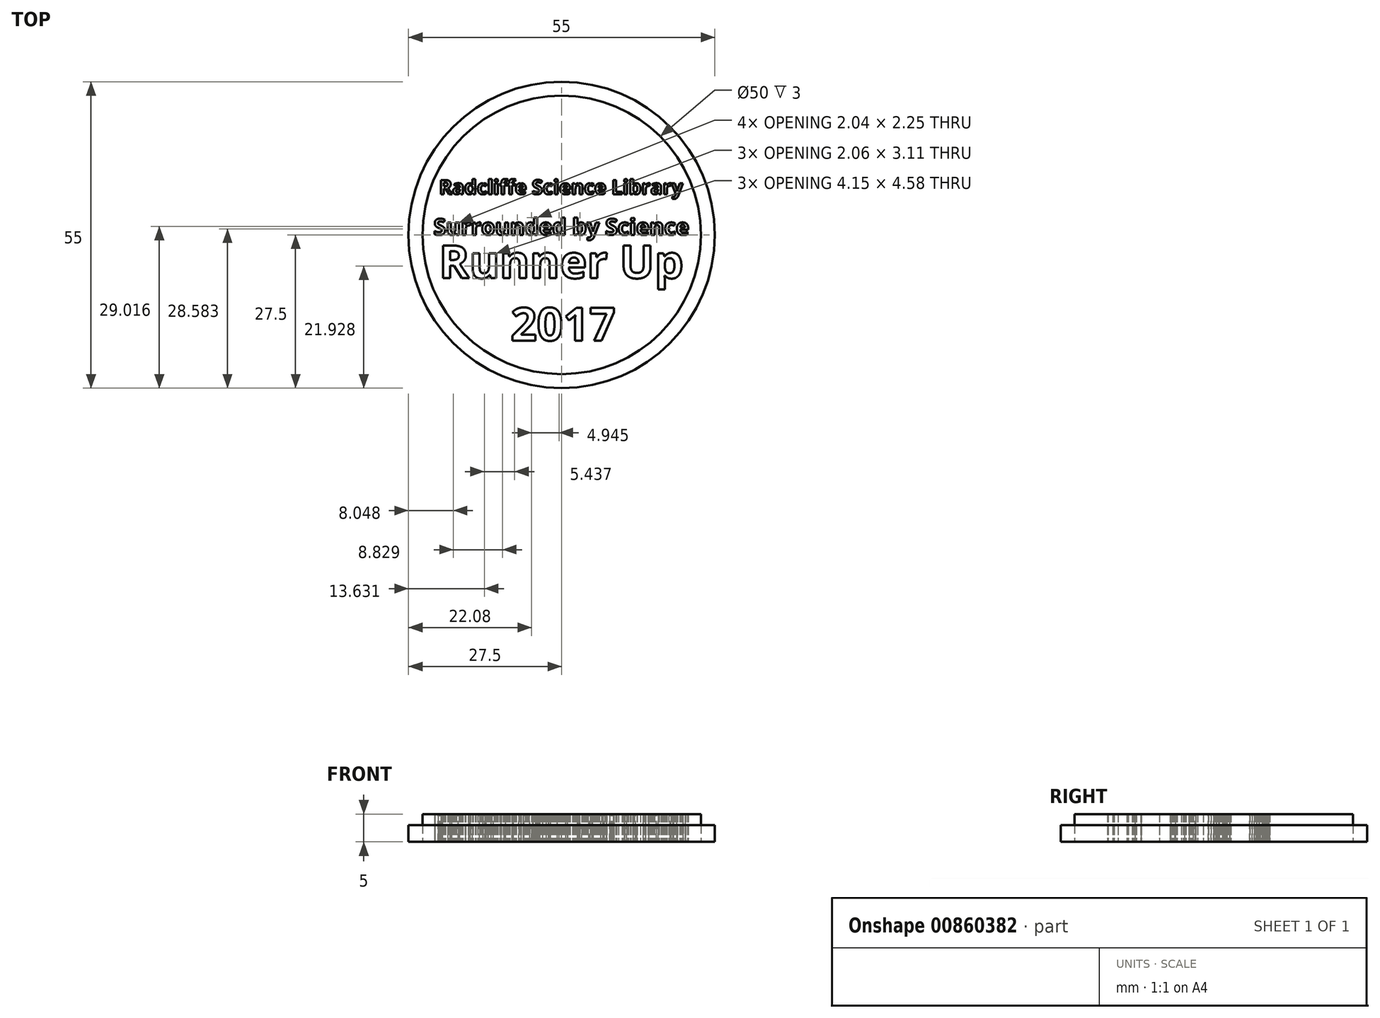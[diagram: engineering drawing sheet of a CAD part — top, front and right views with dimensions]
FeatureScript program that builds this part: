
annotation { "Feature Type Name" : "Feature", "Feature Type Description" : "" }
export const myFeature = defineFeature(function(context is Context, id is Id, definition is map)
    precondition{}
    {
        {
            var Q0;
            Q0=qCreatedBy(makeId("Top.planeOp"),FACE);
            var sketch = newSketch(context, id + "F0", { "sketchPlane" : qUnion([Q0])});
            skCircle(sketch, "E0", {"center": v(0, 0) * mm, "radius": 27.5 * mm});
            skCircle(sketch, "E1", {"center": v(0, 0) * mm, "radius": 25 * mm});
            skText(sketch, "E2", { "text": "Surrounded by Science", "fontName": "OpenSans-Bold.ttf"});
            skText(sketch, "E3", { "text": "Radcliffe Science Library", "fontName": "OpenSans-Bold.ttf"});
            skText(sketch, "E4", { "text": "Runner Up\n      2017     ", "fontName": "OpenSans-Bold.ttf"});
            const initialGuessF0  = {"E2": [-0.023, 0, 1, 0, 0.00291], "E3": [-0.022, 0.0073, 1, 0, 0.00258], "E4": [-0.022, -0.00778, 1, 0, 0.00593]};
            skSetInitialGuess(sketch, initialGuessF0);
            skSolve(sketch);
        }
        {
            var Q0;
            Q0=makeQuery(id+"F0.imprint","IMPRINT",FACE,{"disambiguationData":[TD([[makeQuery(id+"F0.imprint","IMPRINT",EDGE,{"derivedFrom":sQuery(id+"F0.wireOp",EDGE,"E1")}),1.0]])]});
            var Q1;
            Q1=makeQuery(id+"F0.imprint","IMPRINT",FACE,{"disambiguationData":[TD([[makeQuery(id+"F0.imprint","IMPRINT",EDGE,{"derivedFrom":sQuery(id+"F0.wireOp",EDGE,"E4.sketch_text.stroke-173")}),1.0]])]});
            var Q2;
            Q2=makeQuery(id+"F0.imprint","IMPRINT",FACE,{"disambiguationData":[TD([[makeQuery(id+"F0.imprint","IMPRINT",EDGE,{"derivedFrom":sQuery(id+"F0.wireOp",EDGE,"E4.sketch_text.stroke-70")}),1.0]])]});
            var Q3;
            Q3=makeQuery(id+"F0.imprint","IMPRINT",FACE,{"disambiguationData":[TD([[makeQuery(id+"F0.imprint","IMPRINT",EDGE,{"derivedFrom":sQuery(id+"F0.wireOp",EDGE,"E4.sketch_text.stroke-133")}),1.0]])]});
            var Q4;
            Q4=makeQuery(id+"F0.imprint","IMPRINT",FACE,{"disambiguationData":[TD([[makeQuery(id+"F0.imprint","IMPRINT",EDGE,{"derivedFrom":sQuery(id+"F0.wireOp",EDGE,"E4.sketch_text.stroke-0")}),1.0]])]});
            var Q5;
            Q5=makeQuery(id+"F0.imprint","IMPRINT",FACE,{"disambiguationData":[TD([[makeQuery(id+"F0.imprint","IMPRINT",EDGE,{"derivedFrom":sQuery(id+"F0.wireOp",EDGE,"E2.sketch_text.stroke-71")}),1.0]])]});
            var Q6;
            Q6=makeQuery(id+"F0.imprint","IMPRINT",FACE,{"disambiguationData":[TD([[makeQuery(id+"F0.imprint","IMPRINT",EDGE,{"derivedFrom":sQuery(id+"F0.wireOp",EDGE,"E2.sketch_text.stroke-137")}),1.0]])]});
            var Q7;
            Q7=makeQuery(id+"F0.imprint","IMPRINT",FACE,{"disambiguationData":[TD([[makeQuery(id+"F0.imprint","IMPRINT",EDGE,{"derivedFrom":sQuery(id+"F0.wireOp",EDGE,"E2.sketch_text.stroke-146")}),1.0]])]});
            var Q8;
            Q8=makeQuery(id+"F0.imprint","IMPRINT",FACE,{"disambiguationData":[TD([[makeQuery(id+"F0.imprint","IMPRINT",EDGE,{"derivedFrom":sQuery(id+"F0.wireOp",EDGE,"E2.sketch_text.stroke-180")}),1.0]])]});
            var Q9;
            Q9=makeQuery(id+"F0.imprint","IMPRINT",FACE,{"disambiguationData":[TD([[makeQuery(id+"F0.imprint","IMPRINT",EDGE,{"derivedFrom":sQuery(id+"F0.wireOp",EDGE,"E2.sketch_text.stroke-203")}),1.0]])]});
            var Q10;
            Q10=makeQuery(id+"F0.imprint","IMPRINT",FACE,{"disambiguationData":[TD([[makeQuery(id+"F0.imprint","IMPRINT",EDGE,{"derivedFrom":sQuery(id+"F0.wireOp",EDGE,"E2.sketch_text.stroke-280")}),1.0]])]});
            var Q11;
            Q11=makeQuery(id+"F0.imprint","IMPRINT",FACE,{"disambiguationData":[TD([[makeQuery(id+"F0.imprint","IMPRINT",EDGE,{"derivedFrom":sQuery(id+"F0.wireOp",EDGE,"E2.sketch_text.stroke-331")}),1.0]])]});
            var Q12;
            Q12=makeQuery(id+"F0.imprint","IMPRINT",FACE,{"disambiguationData":[TD([[makeQuery(id+"F0.imprint","IMPRINT",EDGE,{"derivedFrom":sQuery(id+"F0.wireOp",EDGE,"E3.sketch_text.stroke-341")}),1.0]])]});
            var Q13;
            Q13=makeQuery(id+"F0.imprint","IMPRINT",FACE,{"disambiguationData":[TD([[makeQuery(id+"F0.imprint","IMPRINT",EDGE,{"derivedFrom":sQuery(id+"F0.wireOp",EDGE,"E3.sketch_text.stroke-301")}),1.0]])]});
            var Q14;
            Q14=makeQuery(id+"F0.imprint","IMPRINT",FACE,{"disambiguationData":[TD([[makeQuery(id+"F0.imprint","IMPRINT",EDGE,{"derivedFrom":sQuery(id+"F0.wireOp",EDGE,"E3.sketch_text.stroke-252")}),1.0]])]});
            var Q15;
            Q15=makeQuery(id+"F0.imprint","IMPRINT",FACE,{"disambiguationData":[TD([[makeQuery(id+"F0.imprint","IMPRINT",EDGE,{"derivedFrom":sQuery(id+"F0.wireOp",EDGE,"E3.sketch_text.stroke-201")}),1.0]])]});
            var Q16;
            Q16=makeQuery(id+"F0.imprint","IMPRINT",FACE,{"disambiguationData":[TD([[makeQuery(id+"F0.imprint","IMPRINT",EDGE,{"derivedFrom":sQuery(id+"F0.wireOp",EDGE,"E3.sketch_text.stroke-130")}),1.0]])]});
            var Q17;
            Q17=makeQuery(id+"F0.imprint","IMPRINT",FACE,{"disambiguationData":[TD([[makeQuery(id+"F0.imprint","IMPRINT",EDGE,{"derivedFrom":sQuery(id+"F0.wireOp",EDGE,"E3.sketch_text.stroke-58")}),1.0]])]});
            var Q18;
            Q18=makeQuery(id+"F0.imprint","IMPRINT",FACE,{"disambiguationData":[TD([[makeQuery(id+"F0.imprint","IMPRINT",EDGE,{"derivedFrom":sQuery(id+"F0.wireOp",EDGE,"E3.sketch_text.stroke-37")}),1.0]])]});
            var Q19;
            Q19=makeQuery(id+"F0.imprint","IMPRINT",FACE,{"disambiguationData":[TD([[makeQuery(id+"F0.imprint","IMPRINT",EDGE,{"derivedFrom":sQuery(id+"F0.wireOp",EDGE,"E3.sketch_text.stroke-0")}),1.0]])]});
            extrude(context, id + "F1", {"entities" : qUnion([Q0, Q1, Q2, Q3, Q4, Q5, Q6, Q7, Q8, Q9, Q10, Q11, Q12, Q13, Q14, Q15, Q16, Q17, Q18, Q19]), "depth" : 5 * mm, "offsetDistance" : 25 * mm});
        }
        {
            var Q0;
            Q0=makeQuery(id+"F0.imprint","IMPRINT",FACE,{"disambiguationData":[TD([[makeQuery(id+"F0.imprint","IMPRINT",EDGE,{"derivedFrom":sQuery(id+"F0.wireOp",EDGE,"E0")}),1.0]])]});
            var Q1;
            Q1=makeQuery(id+"F0.imprint","IMPRINT",FACE,{"disambiguationData":[TD([[makeQuery(id+"F0.imprint","IMPRINT",EDGE,{"derivedFrom":sQuery(id+"F0.wireOp",EDGE,"E4.sketch_text.stroke-141")}),-1.0]])]});
            var Q2;
            Q2=makeQuery(id+"F0.imprint","IMPRINT",FACE,{"disambiguationData":[TD([[makeQuery(id+"F0.imprint","IMPRINT",EDGE,{"derivedFrom":sQuery(id+"F0.wireOp",EDGE,"E4.sketch_text.stroke-165")}),-1.0]])]});
            var Q3;
            Q3=makeQuery(id+"F0.imprint","IMPRINT",FACE,{"disambiguationData":[TD([[makeQuery(id+"F0.imprint","IMPRINT",EDGE,{"derivedFrom":sQuery(id+"F0.wireOp",EDGE,"E4.sketch_text.stroke-181")}),-1.0]])]});
            var Q4;
            Q4=makeQuery(id+"F0.imprint","IMPRINT",FACE,{"disambiguationData":[TD([[makeQuery(id+"F0.imprint","IMPRINT",EDGE,{"derivedFrom":sQuery(id+"F0.wireOp",EDGE,"E4.sketch_text.stroke-191")}),-1.0]])]});
            var Q5;
            Q5=makeQuery(id+"F0.imprint","IMPRINT",FACE,{"disambiguationData":[TD([[makeQuery(id+"F0.imprint","IMPRINT",EDGE,{"derivedFrom":sQuery(id+"F0.wireOp",EDGE,"E4.sketch_text.stroke-118")}),-1.0]])]});
            var Q6;
            Q6=makeQuery(id+"F0.imprint","IMPRINT",FACE,{"disambiguationData":[TD([[makeQuery(id+"F0.imprint","IMPRINT",EDGE,{"derivedFrom":sQuery(id+"F0.wireOp",EDGE,"E4.sketch_text.stroke-103")}),-1.0]])]});
            var Q7;
            Q7=makeQuery(id+"F0.imprint","IMPRINT",FACE,{"disambiguationData":[TD([[makeQuery(id+"F0.imprint","IMPRINT",EDGE,{"derivedFrom":sQuery(id+"F0.wireOp",EDGE,"E4.sketch_text.stroke-90")}),-1.0]])]});
            var Q8;
            Q8=makeQuery(id+"F0.imprint","IMPRINT",FACE,{"disambiguationData":[TD([[makeQuery(id+"F0.imprint","IMPRINT",EDGE,{"derivedFrom":sQuery(id+"F0.wireOp",EDGE,"E4.sketch_text.stroke-70")}),-1.0]])]});
            var Q9;
            Q9=makeQuery(id+"F0.imprint","IMPRINT",FACE,{"disambiguationData":[TD([[makeQuery(id+"F0.imprint","IMPRINT",EDGE,{"derivedFrom":sQuery(id+"F0.wireOp",EDGE,"E4.sketch_text.stroke-53")}),-1.0]])]});
            var Q10;
            Q10=makeQuery(id+"F0.imprint","IMPRINT",FACE,{"disambiguationData":[TD([[makeQuery(id+"F0.imprint","IMPRINT",EDGE,{"derivedFrom":sQuery(id+"F0.wireOp",EDGE,"E4.sketch_text.stroke-36")}),-1.0]])]});
            var Q11;
            Q11=makeQuery(id+"F0.imprint","IMPRINT",FACE,{"disambiguationData":[TD([[makeQuery(id+"F0.imprint","IMPRINT",EDGE,{"derivedFrom":sQuery(id+"F0.wireOp",EDGE,"E4.sketch_text.stroke-19")}),-1.0]])]});
            var Q12;
            Q12=makeQuery(id+"F0.imprint","IMPRINT",FACE,{"disambiguationData":[TD([[makeQuery(id+"F0.imprint","IMPRINT",EDGE,{"derivedFrom":sQuery(id+"F0.wireOp",EDGE,"E4.sketch_text.stroke-0")}),-1.0]])]});
            var Q13;
            Q13=makeQuery(id+"F0.imprint","IMPRINT",FACE,{"disambiguationData":[TD([[makeQuery(id+"F0.imprint","IMPRINT",EDGE,{"derivedFrom":sQuery(id+"F0.wireOp",EDGE,"E2.sketch_text.stroke-0")}),-1.0]])]});
            var Q14;
            Q14=makeQuery(id+"F0.imprint","IMPRINT",FACE,{"disambiguationData":[TD([[makeQuery(id+"F0.imprint","IMPRINT",EDGE,{"derivedFrom":sQuery(id+"F0.wireOp",EDGE,"E2.sketch_text.stroke-28")}),-1.0]])]});
            var Q15;
            Q15=makeQuery(id+"F0.imprint","IMPRINT",FACE,{"disambiguationData":[TD([[makeQuery(id+"F0.imprint","IMPRINT",EDGE,{"derivedFrom":sQuery(id+"F0.wireOp",EDGE,"E2.sketch_text.stroke-45")}),-1.0]])]});
            var Q16;
            Q16=makeQuery(id+"F0.imprint","IMPRINT",FACE,{"disambiguationData":[TD([[makeQuery(id+"F0.imprint","IMPRINT",EDGE,{"derivedFrom":sQuery(id+"F0.wireOp",EDGE,"E2.sketch_text.stroke-58")}),-1.0]])]});
            var Q17;
            Q17=makeQuery(id+"F0.imprint","IMPRINT",FACE,{"disambiguationData":[TD([[makeQuery(id+"F0.imprint","IMPRINT",EDGE,{"derivedFrom":sQuery(id+"F0.wireOp",EDGE,"E2.sketch_text.stroke-71")}),-1.0]])]});
            var Q18;
            Q18=makeQuery(id+"F0.imprint","IMPRINT",FACE,{"disambiguationData":[TD([[makeQuery(id+"F0.imprint","IMPRINT",EDGE,{"derivedFrom":sQuery(id+"F0.wireOp",EDGE,"E2.sketch_text.stroke-89")}),-1.0]])]});
            var Q19;
            Q19=makeQuery(id+"F0.imprint","IMPRINT",FACE,{"disambiguationData":[TD([[makeQuery(id+"F0.imprint","IMPRINT",EDGE,{"derivedFrom":sQuery(id+"F0.wireOp",EDGE,"E2.sketch_text.stroke-106")}),-1.0]])]});
            var Q20;
            Q20=makeQuery(id+"F0.imprint","IMPRINT",FACE,{"disambiguationData":[TD([[makeQuery(id+"F0.imprint","IMPRINT",EDGE,{"derivedFrom":sQuery(id+"F0.wireOp",EDGE,"E2.sketch_text.stroke-123")}),-1.0]])]});
            var Q21;
            Q21=makeQuery(id+"F0.imprint","IMPRINT",FACE,{"disambiguationData":[TD([[makeQuery(id+"F0.imprint","IMPRINT",EDGE,{"derivedFrom":sQuery(id+"F0.wireOp",EDGE,"E2.sketch_text.stroke-146")}),-1.0]])]});
            var Q22;
            Q22=makeQuery(id+"F0.imprint","IMPRINT",FACE,{"disambiguationData":[TD([[makeQuery(id+"F0.imprint","IMPRINT",EDGE,{"derivedFrom":sQuery(id+"F0.wireOp",EDGE,"E2.sketch_text.stroke-166")}),-1.0]])]});
            var Q23;
            Q23=makeQuery(id+"F0.imprint","IMPRINT",FACE,{"disambiguationData":[TD([[makeQuery(id+"F0.imprint","IMPRINT",EDGE,{"derivedFrom":sQuery(id+"F0.wireOp",EDGE,"E2.sketch_text.stroke-189")}),-1.0]])]});
            var Q24;
            Q24=makeQuery(id+"F0.imprint","IMPRINT",FACE,{"disambiguationData":[TD([[makeQuery(id+"F0.imprint","IMPRINT",EDGE,{"derivedFrom":sQuery(id+"F0.wireOp",EDGE,"E2.sketch_text.stroke-212")}),-1.0]])]});
            var Q25;
            Q25=makeQuery(id+"F0.imprint","IMPRINT",FACE,{"disambiguationData":[TD([[makeQuery(id+"F0.imprint","IMPRINT",EDGE,{"derivedFrom":sQuery(id+"F0.wireOp",EDGE,"E2.sketch_text.stroke-229")}),-1.0]])]});
            var Q26;
            Q26=makeQuery(id+"F0.imprint","IMPRINT",FACE,{"disambiguationData":[TD([[makeQuery(id+"F0.imprint","IMPRINT",EDGE,{"derivedFrom":sQuery(id+"F0.wireOp",EDGE,"E2.sketch_text.stroke-257")}),-1.0]])]});
            var Q27;
            Q27=makeQuery(id+"F0.imprint","IMPRINT",FACE,{"disambiguationData":[TD([[makeQuery(id+"F0.imprint","IMPRINT",EDGE,{"derivedFrom":sQuery(id+"F0.wireOp",EDGE,"E2.sketch_text.stroke-271")}),-1.0]])]});
            var Q28;
            Q28=makeQuery(id+"F0.imprint","IMPRINT",FACE,{"disambiguationData":[TD([[makeQuery(id+"F0.imprint","IMPRINT",EDGE,{"derivedFrom":sQuery(id+"F0.wireOp",EDGE,"E2.sketch_text.stroke-280")}),-1.0]])]});
            var Q29;
            Q29=makeQuery(id+"F0.imprint","IMPRINT",FACE,{"disambiguationData":[TD([[makeQuery(id+"F0.imprint","IMPRINT",EDGE,{"derivedFrom":sQuery(id+"F0.wireOp",EDGE,"E2.sketch_text.stroke-300")}),-1.0]])]});
            var Q30;
            Q30=makeQuery(id+"F0.imprint","IMPRINT",FACE,{"disambiguationData":[TD([[makeQuery(id+"F0.imprint","IMPRINT",EDGE,{"derivedFrom":sQuery(id+"F0.wireOp",EDGE,"E2.sketch_text.stroke-317")}),-1.0]])]});
            var Q31;
            Q31=makeQuery(id+"F0.imprint","IMPRINT",FACE,{"disambiguationData":[TD([[makeQuery(id+"F0.imprint","IMPRINT",EDGE,{"derivedFrom":sQuery(id+"F0.wireOp",EDGE,"E2.sketch_text.stroke-331")}),-1.0]])]});
            var Q32;
            Q32=makeQuery(id+"F0.imprint","IMPRINT",FACE,{"disambiguationData":[TD([[makeQuery(id+"F0.imprint","IMPRINT",EDGE,{"derivedFrom":sQuery(id+"F0.wireOp",EDGE,"E2.sketch_text.stroke-276")}),-1.0]])]});
            var Q33;
            Q33=makeQuery(id+"F0.imprint","IMPRINT",FACE,{"disambiguationData":[TD([[makeQuery(id+"F0.imprint","IMPRINT",EDGE,{"derivedFrom":sQuery(id+"F0.wireOp",EDGE,"E3.sketch_text.stroke-361")}),-1.0]])]});
            var Q34;
            Q34=makeQuery(id+"F0.imprint","IMPRINT",FACE,{"disambiguationData":[TD([[makeQuery(id+"F0.imprint","IMPRINT",EDGE,{"derivedFrom":sQuery(id+"F0.wireOp",EDGE,"E3.sketch_text.stroke-348")}),-1.0]])]});
            var Q35;
            Q35=makeQuery(id+"F0.imprint","IMPRINT",FACE,{"disambiguationData":[TD([[makeQuery(id+"F0.imprint","IMPRINT",EDGE,{"derivedFrom":sQuery(id+"F0.wireOp",EDGE,"E3.sketch_text.stroke-323")}),-1.0]])]});
            var Q36;
            Q36=makeQuery(id+"F0.imprint","IMPRINT",FACE,{"disambiguationData":[TD([[makeQuery(id+"F0.imprint","IMPRINT",EDGE,{"derivedFrom":sQuery(id+"F0.wireOp",EDGE,"E3.sketch_text.stroke-310")}),-1.0]])]});
            var Q37;
            Q37=makeQuery(id+"F0.imprint","IMPRINT",FACE,{"disambiguationData":[TD([[makeQuery(id+"F0.imprint","IMPRINT",EDGE,{"derivedFrom":sQuery(id+"F0.wireOp",EDGE,"E3.sketch_text.stroke-287")}),-1.0]])]});
            var Q38;
            Q38=makeQuery(id+"F0.imprint","IMPRINT",FACE,{"disambiguationData":[TD([[makeQuery(id+"F0.imprint","IMPRINT",EDGE,{"derivedFrom":sQuery(id+"F0.wireOp",EDGE,"E3.sketch_text.stroke-283")}),-1.0]])]});
            var Q39;
            Q39=makeQuery(id+"F0.imprint","IMPRINT",FACE,{"disambiguationData":[TD([[makeQuery(id+"F0.imprint","IMPRINT",EDGE,{"derivedFrom":sQuery(id+"F0.wireOp",EDGE,"E3.sketch_text.stroke-272")}),-1.0]])]});
            var Q40;
            Q40=makeQuery(id+"F0.imprint","IMPRINT",FACE,{"disambiguationData":[TD([[makeQuery(id+"F0.imprint","IMPRINT",EDGE,{"derivedFrom":sQuery(id+"F0.wireOp",EDGE,"E3.sketch_text.stroke-252")}),-1.0]])]});
            var Q41;
            Q41=makeQuery(id+"F0.imprint","IMPRINT",FACE,{"disambiguationData":[TD([[makeQuery(id+"F0.imprint","IMPRINT",EDGE,{"derivedFrom":sQuery(id+"F0.wireOp",EDGE,"E3.sketch_text.stroke-278")}),-1.0]])]});
            var Q42;
            Q42=makeQuery(id+"F0.imprint","IMPRINT",FACE,{"disambiguationData":[TD([[makeQuery(id+"F0.imprint","IMPRINT",EDGE,{"derivedFrom":sQuery(id+"F0.wireOp",EDGE,"E3.sketch_text.stroke-238")}),-1.0]])]});
            var Q43;
            Q43=makeQuery(id+"F0.imprint","IMPRINT",FACE,{"disambiguationData":[TD([[makeQuery(id+"F0.imprint","IMPRINT",EDGE,{"derivedFrom":sQuery(id+"F0.wireOp",EDGE,"E3.sketch_text.stroke-221")}),-1.0]])]});
            var Q44;
            Q44=makeQuery(id+"F0.imprint","IMPRINT",FACE,{"disambiguationData":[TD([[makeQuery(id+"F0.imprint","IMPRINT",EDGE,{"derivedFrom":sQuery(id+"F0.wireOp",EDGE,"E3.sketch_text.stroke-201")}),-1.0]])]});
            var Q45;
            Q45=makeQuery(id+"F0.imprint","IMPRINT",FACE,{"disambiguationData":[TD([[makeQuery(id+"F0.imprint","IMPRINT",EDGE,{"derivedFrom":sQuery(id+"F0.wireOp",EDGE,"E3.sketch_text.stroke-197")}),-1.0]])]});
            var Q46;
            Q46=makeQuery(id+"F0.imprint","IMPRINT",FACE,{"disambiguationData":[TD([[makeQuery(id+"F0.imprint","IMPRINT",EDGE,{"derivedFrom":sQuery(id+"F0.wireOp",EDGE,"E3.sketch_text.stroke-192")}),-1.0]])]});
            var Q47;
            Q47=makeQuery(id+"F0.imprint","IMPRINT",FACE,{"disambiguationData":[TD([[makeQuery(id+"F0.imprint","IMPRINT",EDGE,{"derivedFrom":sQuery(id+"F0.wireOp",EDGE,"E3.sketch_text.stroke-178")}),-1.0]])]});
            var Q48;
            Q48=makeQuery(id+"F0.imprint","IMPRINT",FACE,{"disambiguationData":[TD([[makeQuery(id+"F0.imprint","IMPRINT",EDGE,{"derivedFrom":sQuery(id+"F0.wireOp",EDGE,"E3.sketch_text.stroke-150")}),-1.0]])]});
            var Q49;
            Q49=makeQuery(id+"F0.imprint","IMPRINT",FACE,{"disambiguationData":[TD([[makeQuery(id+"F0.imprint","IMPRINT",EDGE,{"derivedFrom":sQuery(id+"F0.wireOp",EDGE,"E3.sketch_text.stroke-130")}),-1.0]])]});
            var Q50;
            Q50=makeQuery(id+"F0.imprint","IMPRINT",FACE,{"disambiguationData":[TD([[makeQuery(id+"F0.imprint","IMPRINT",EDGE,{"derivedFrom":sQuery(id+"F0.wireOp",EDGE,"E3.sketch_text.stroke-94")}),-1.0]])]});
            var Q51;
            Q51=makeQuery(id+"F0.imprint","IMPRINT",FACE,{"disambiguationData":[TD([[makeQuery(id+"F0.imprint","IMPRINT",EDGE,{"derivedFrom":sQuery(id+"F0.wireOp",EDGE,"E3.sketch_text.stroke-90")}),-1.0]])]});
            var Q52;
            Q52=makeQuery(id+"F0.imprint","IMPRINT",FACE,{"disambiguationData":[TD([[makeQuery(id+"F0.imprint","IMPRINT",EDGE,{"derivedFrom":sQuery(id+"F0.wireOp",EDGE,"E3.sketch_text.stroke-112")}),-1.0]])]});
            var Q53;
            Q53=makeQuery(id+"F0.imprint","IMPRINT",FACE,{"disambiguationData":[TD([[makeQuery(id+"F0.imprint","IMPRINT",EDGE,{"derivedFrom":sQuery(id+"F0.wireOp",EDGE,"E3.sketch_text.stroke-85")}),-1.0]])]});
            var Q54;
            Q54=makeQuery(id+"F0.imprint","IMPRINT",FACE,{"disambiguationData":[TD([[makeQuery(id+"F0.imprint","IMPRINT",EDGE,{"derivedFrom":sQuery(id+"F0.wireOp",EDGE,"E3.sketch_text.stroke-81")}),-1.0]])]});
            var Q55;
            Q55=makeQuery(id+"F0.imprint","IMPRINT",FACE,{"disambiguationData":[TD([[makeQuery(id+"F0.imprint","IMPRINT",EDGE,{"derivedFrom":sQuery(id+"F0.wireOp",EDGE,"E3.sketch_text.stroke-67")}),-1.0]])]});
            var Q56;
            Q56=makeQuery(id+"F0.imprint","IMPRINT",FACE,{"disambiguationData":[TD([[makeQuery(id+"F0.imprint","IMPRINT",EDGE,{"derivedFrom":sQuery(id+"F0.wireOp",EDGE,"E3.sketch_text.stroke-19")}),-1.0]])]});
            var Q57;
            Q57=makeQuery(id+"F0.imprint","IMPRINT",FACE,{"disambiguationData":[TD([[makeQuery(id+"F0.imprint","IMPRINT",EDGE,{"derivedFrom":sQuery(id+"F0.wireOp",EDGE,"E3.sketch_text.stroke-0")}),-1.0]])]});
            var Q58;
            Q58=makeQuery(id+"F0.imprint","IMPRINT",FACE,{"disambiguationData":[TD([[makeQuery(id+"F0.imprint","IMPRINT",EDGE,{"derivedFrom":sQuery(id+"F0.wireOp",EDGE,"E3.sketch_text.stroke-44")}),-1.0]])]});
            extrude(context, id + "F2", {"entities" : qUnion([Q0, Q1, Q2, Q3, Q4, Q5, Q6, Q7, Q8, Q9, Q10, Q11, Q12, Q13, Q14, Q15, Q16, Q17, Q18, Q19, Q20, Q21, Q22, Q23, Q24, Q25, Q26, Q27, Q28, Q29, Q30, Q31, Q32, Q33, Q34, Q35, Q36, Q37, Q38, Q39, Q40, Q41, Q42, Q43, Q44, Q45, Q46, Q47, Q48, Q49, Q50, Q51, Q52, Q53, Q54, Q55, Q56, Q57, Q58]), "depth" : 3 * mm, "offsetDistance" : 25 * mm});
        }
    });
